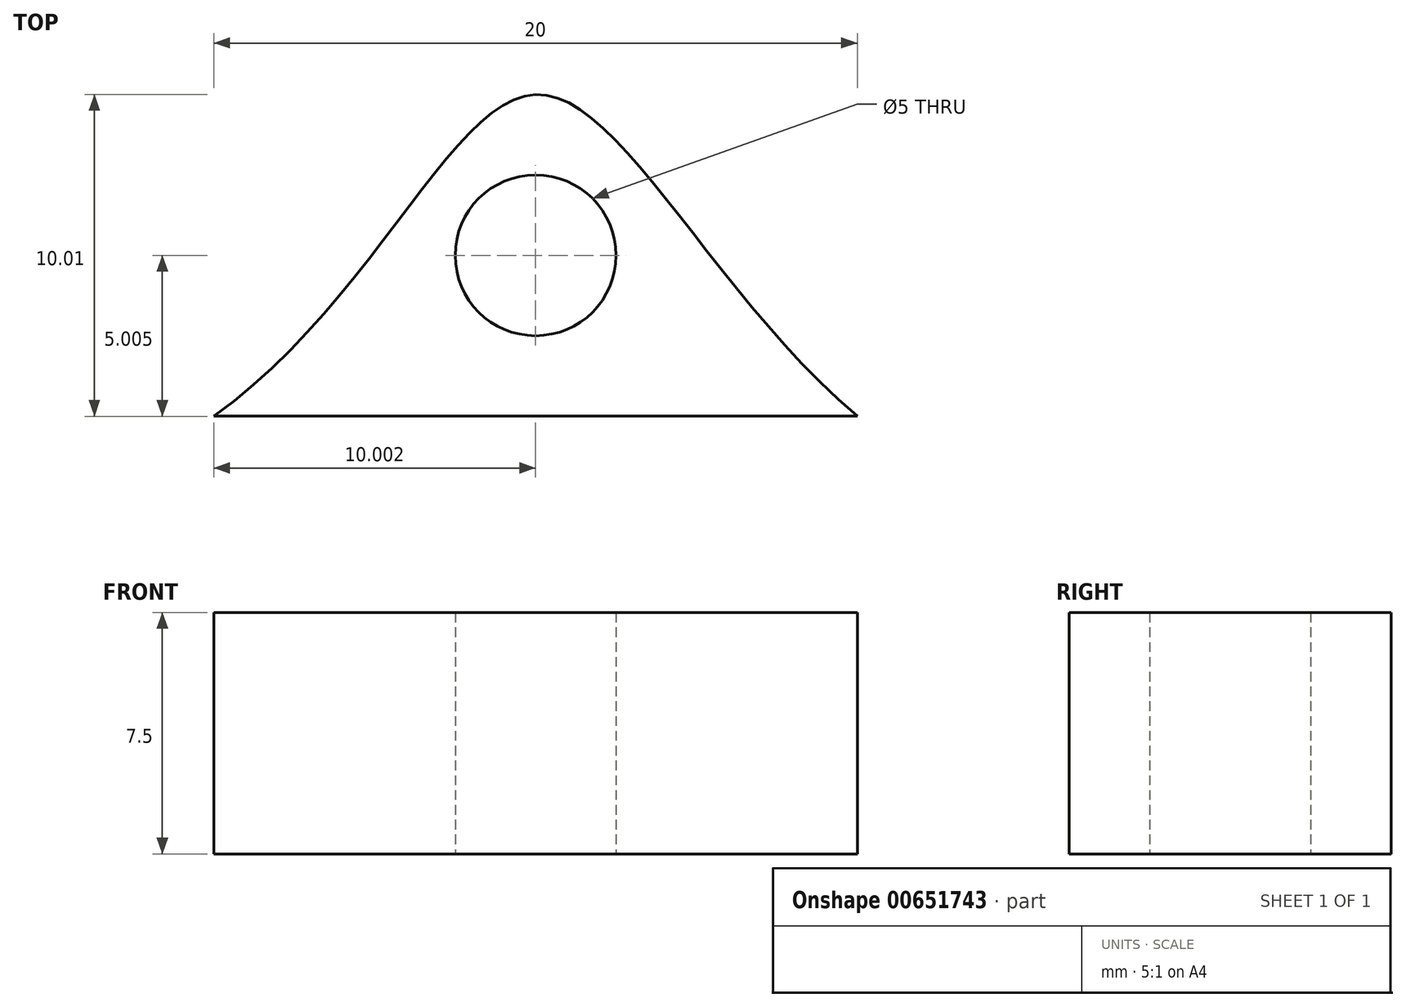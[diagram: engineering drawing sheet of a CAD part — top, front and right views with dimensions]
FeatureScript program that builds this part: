
annotation { "Feature Type Name" : "Feature", "Feature Type Description" : "" }
export const myFeature = defineFeature(function(context is Context, id is Id, definition is map)
    precondition{}
    {
        {
            var Q0;
            Q0=qCreatedBy(makeId("Top.planeOp"),FACE);
            var sketch = newSketch(context, id + "F0", { "sketchPlane" : qUnion([Q0])});
            skLineSegment(sketch, "E0", {"start": v(-27.69, -12.39) * mm, "end": v(-7.69, -12.39) * mm});
            skLineSegment(sketch, "E1", {"start": v(-17.69, -12.39) * mm, "end": v(-17.69, -2.39) * mm});
            skFitSpline(sketch, "E2", {"points": [v(-27.69, -12.39) * mm, v(-17.69, -2.39) * mm, v(-7.69, -12.39) * mm], "startDerivative": vector(29.7, 21.15) * mm, "endDerivative": vector(27.77, -23.62) * mm});
            skCircle(sketch, "E3", {"center": v(-17.69, -7.39) * mm, "radius": 2.5 * mm});
            skSolve(sketch);
        }
        {
            var Q0;
            {var subQ0=sQuery(id+"F0.wireOp",EDGE,"E2");var subQ5=sQuery(id+"F0.wireOp",EDGE,"E0");var subQ8=makeQuery(id+"F0.imprint","INTERSECT",VERTEX,{"disambiguationData":[OD(0.0)],"derivedFrom":[subQ5,subQ0]});Q0=makeQuery(id+"F0.imprint","IMPRINT",FACE,{"disambiguationData":[TD([[makeQuery(id+"F0.imprint","IMPRINT",EDGE,{"disambiguationData":[TD([[subQ8,-1.0]])],"derivedFrom":subQ5}),1.0]])]});}
            var Q1;
            {var subQ0=sQuery(id+"F0.wireOp",EDGE,"E2");var subQ5=sQuery(id+"F0.wireOp",EDGE,"E0");var subQ8=makeQuery(id+"F0.imprint","INTERSECT",VERTEX,{"disambiguationData":[OD(1.0)],"derivedFrom":[subQ5,subQ0]});Q1=makeQuery(id+"F0.imprint","IMPRINT",FACE,{"disambiguationData":[TD([[makeQuery(id+"F0.imprint","IMPRINT",EDGE,{"disambiguationData":[TD([[subQ8,1.0]])],"derivedFrom":subQ5}),1.0]])]});}
            extrude(context, id + "F1", {"entities" : qUnion([Q0, Q1]), "depth" : 7.5 * mm, "offsetDistance" : 25 * mm});
        }
    });
